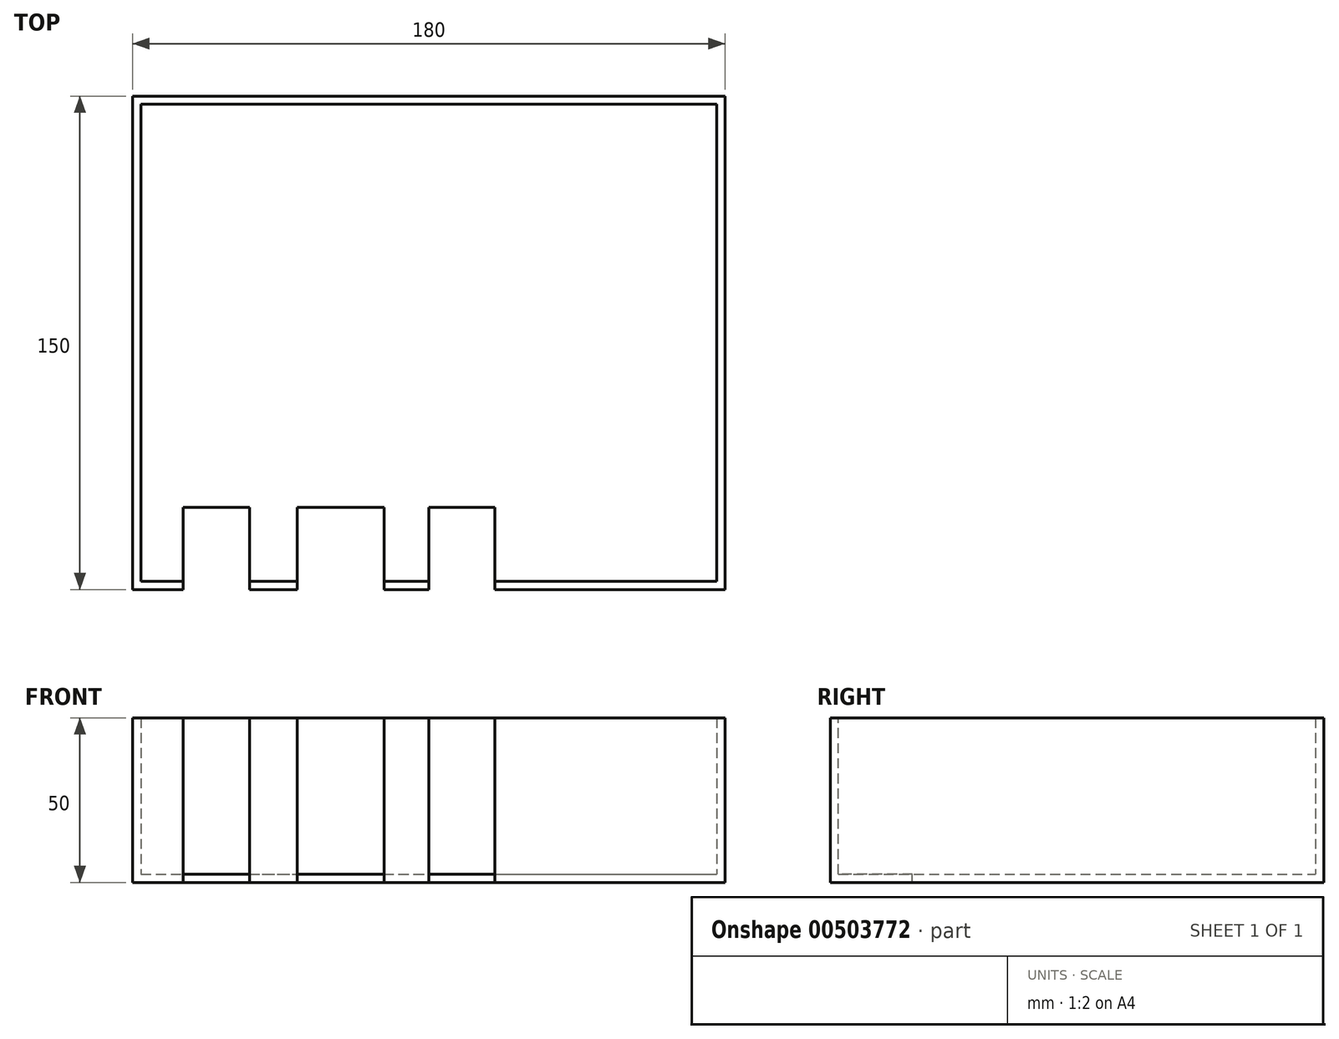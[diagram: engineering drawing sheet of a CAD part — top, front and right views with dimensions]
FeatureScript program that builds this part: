
annotation { "Feature Type Name" : "Feature", "Feature Type Description" : "" }
export const myFeature = defineFeature(function(context is Context, id is Id, definition is map)
    precondition{}
    {
        {
            var Q0;
            Q0=qCreatedBy(makeId("Top.planeOp"),FACE);
            var sketch = newSketch(context, id + "F0", { "sketchPlane" : qUnion([Q0])});
            skLineSegment(sketch, "E0.bottom", {"start": v(-90, -75) * mm, "end": v(90, -75) * mm});
            skLineSegment(sketch, "E0.top", {"start": v(-90, 75) * mm, "end": v(90, 75) * mm});
            skLineSegment(sketch, "E0.left", {"start": v(-90, -75) * mm, "end": v(-90, 75) * mm});
            skLineSegment(sketch, "E0.right", {"start": v(90, -75) * mm, "end": v(90, 75) * mm});
            skPoint(sketch, "E0.middle", {"position": v(0, 0) * mm});
            skSolve(sketch);
        }
        {
            var Q0;
            Q0=makeQuery(id+"F0.imprint","IMPRINT",FACE,{"disambiguationData":[TD([[makeQuery(id+"F0.imprint","IMPRINT",EDGE,{"derivedFrom":sQuery(id+"F0.wireOp",EDGE,"E0.bottom")}),1.0]])]});
            extrude(context, id + "F1", {"entities" : qUnion([Q0]), "depth" : 50 * mm});
        }
        {
            var Q0;
            Q0=makeQuery(id+"F1.opExtrude","CAP_FACE",FACE,{"disambiguationData":[OSD([sQuery(id+"F0.wireOp",EDGE,"E0.bottom"),sQuery(id+"F0.wireOp",EDGE,"E0.top"),sQuery(id+"F0.wireOp",EDGE,"E0.left"),sQuery(id+"F0.wireOp",EDGE,"E0.right")])],"isStart":false});
            shell(context, id + "F2", {"entities" : qUnion([Q0]), "thickness" : 2.5 * mm});
        }
        {
            var Q0;
            Q0=makeQuery(id+"F1.opExtrude","SWEPT_FACE",FACE,{"disambiguationData":[OSD([sQuery(id+"F0.wireOp",EDGE,"E0.bottom")])]});
            var sketch = newSketch(context, id + "F3", { "sketchPlane" : qUnion([Q0])});
            skLineSegment(sketch, "E1.bottom", {"start": v(-74.6, 0) * mm, "end": v(-54.47, 0) * mm});
            skLineSegment(sketch, "E1.top", {"start": v(-74.6, 50) * mm, "end": v(-54.47, 50) * mm});
            skLineSegment(sketch, "E1.left", {"start": v(-74.6, 0) * mm, "end": v(-74.6, 50) * mm});
            skLineSegment(sketch, "E1.right", {"start": v(-54.47, 0) * mm, "end": v(-54.47, 50) * mm});
            skSolve(sketch);
        }
        {
            var Q0;
            Q0=makeQuery(id+"F3.imprint","IMPRINT",FACE,{"disambiguationData":[TD([[makeQuery(id+"F3.imprint","IMPRINT",EDGE,{"derivedFrom":sQuery(id+"F3.wireOp",EDGE,"E1.bottom")}),1.0]])]});
            extrude(context, id + "F4", {"entities" : qUnion([Q0]), "operationType" : NewBodyOperationType.REMOVE, "oppositeDirection" : true, "depth" : 25 * mm});
        }
        {
            var Q0;
            {var subQ0=sQuery(id+"F0.wireOp",EDGE,"E0.right");var subQ3=sQuery(id+"F0.wireOp",EDGE,"E0.bottom");Q0=makeQuery(id+"F4.boolean.opBoolean","SPLIT",FACE,{"disambiguationData":[TD([makeQuery(id+"F1.opExtrude","SWEPT_FACE",FACE,{"disambiguationData":[OSD([subQ0])]})])],"derivedFrom":makeQuery(id+"F1.opExtrude","SWEPT_FACE",FACE,{"disambiguationData":[OSD([subQ3])]})});}
            var sketch = newSketch(context, id + "F5", { "sketchPlane" : qUnion([Q0])});
            skLineSegment(sketch, "E2.bottom", {"start": v(-39.97, 0) * mm, "end": v(-19.84, 0) * mm});
            skLineSegment(sketch, "E2.top", {"start": v(-39.97, 50) * mm, "end": v(-19.84, 50) * mm});
            skLineSegment(sketch, "E2.left", {"start": v(-39.97, 0) * mm, "end": v(-39.97, 50) * mm});
            skLineSegment(sketch, "E2.right", {"start": v(-19.84, 0) * mm, "end": v(-19.84, 50) * mm});
            skSolve(sketch);
        }
        {
            var Q0;
            Q0=makeQuery(id+"F5.imprint","IMPRINT",FACE,{"disambiguationData":[TD([[makeQuery(id+"F5.imprint","IMPRINT",EDGE,{"derivedFrom":sQuery(id+"F5.wireOp",EDGE,"E2.bottom")}),1.0]])]});
            extrude(context, id + "F6", {"entities" : qUnion([Q0]), "operationType" : NewBodyOperationType.REMOVE, "oppositeDirection" : true, "depth" : 25 * mm});
        }
        {
            var Q0;
            {var subQ0=sQuery(id+"F0.wireOp",EDGE,"E0.right");var subQ3=sQuery(id+"F0.wireOp",EDGE,"E0.bottom");var subQ6=makeQuery(id+"F1.opExtrude","SWEPT_FACE",FACE,{"disambiguationData":[OSD([subQ0])]});Q0=makeQuery(id+"F6.boolean.opBoolean","SPLIT",FACE,{"disambiguationData":[TD([subQ6])],"derivedFrom":makeQuery(id+"F4.boolean.opBoolean","SPLIT",FACE,{"disambiguationData":[TD([subQ6])],"derivedFrom":makeQuery(id+"F1.opExtrude","SWEPT_FACE",FACE,{"disambiguationData":[OSD([subQ3])]})})});}
            var sketch = newSketch(context, id + "F7", { "sketchPlane" : qUnion([Q0])});
            skLineSegment(sketch, "E3.bottom", {"start": v(0, 0) * mm, "end": v(20.13, 0) * mm});
            skLineSegment(sketch, "E3.top", {"start": v(0, 50) * mm, "end": v(20.13, 50) * mm});
            skLineSegment(sketch, "E3.left", {"start": v(0, 0) * mm, "end": v(0, 50) * mm});
            skLineSegment(sketch, "E3.right", {"start": v(20.13, 0) * mm, "end": v(20.13, 50) * mm});
            skSolve(sketch);
        }
        {
            var Q0;
            Q0 = qSketchRegion(id + "F7", true);
            extrude(context, id + "F8", {"entities" : qUnion([Q0]), "operationType" : NewBodyOperationType.REMOVE, "oppositeDirection" : true, "depth" : 25 * mm});
        }
        {
            var Q0;
            {var subQ0=sQuery(id+"F0.wireOp",EDGE,"E0.right");var subQ3=sQuery(id+"F0.wireOp",EDGE,"E0.bottom");var subQ5=makeQuery(id+"F6.opExtrude","SWEPT_FACE",FACE,{"disambiguationData":[OSD([sQuery(id+"F5.wireOp",EDGE,"E2.right")])]});var subQ7=makeQuery(id+"F1.opExtrude","SWEPT_FACE",FACE,{"disambiguationData":[OSD([subQ0])]});Q0=makeQuery(id+"F8.boolean.opBoolean","SPLIT",FACE,{"disambiguationData":[TD([makeQuery(id+"F6.boolean.opBoolean","COPY",FACE,{"derivedFrom":subQ5})])],"derivedFrom":makeQuery(id+"F6.boolean.opBoolean","SPLIT",FACE,{"disambiguationData":[TD([subQ7])],"derivedFrom":makeQuery(id+"F4.boolean.opBoolean","SPLIT",FACE,{"disambiguationData":[TD([subQ7])],"derivedFrom":makeQuery(id+"F1.opExtrude","SWEPT_FACE",FACE,{"disambiguationData":[OSD([subQ3])]})})})});}
            var sketch = newSketch(context, id + "F9", { "sketchPlane" : qUnion([Q0])});
            skLineSegment(sketch, "E4.bottom", {"start": v(-19.84, 50) * mm, "end": v(-13.62, 50) * mm});
            skLineSegment(sketch, "E4.top", {"start": v(-19.84, 0) * mm, "end": v(-13.62, 0) * mm});
            skLineSegment(sketch, "E4.left", {"start": v(-19.84, 50) * mm, "end": v(-19.84, 0) * mm});
            skLineSegment(sketch, "E4.right", {"start": v(-13.62, 50) * mm, "end": v(-13.62, 0) * mm});
            skSolve(sketch);
        }
        {
            var Q0;
            Q0=makeQuery(id+"F9.imprint","IMPRINT",FACE,{"disambiguationData":[TD([[makeQuery(id+"F9.imprint","IMPRINT",EDGE,{"derivedFrom":sQuery(id+"F9.wireOp",EDGE,"E4.bottom")}),-1.0]])]});
            extrude(context, id + "F10", {"entities" : qUnion([Q0]), "operationType" : NewBodyOperationType.REMOVE, "oppositeDirection" : true, "depth" : 25 * mm});
        }
    });
